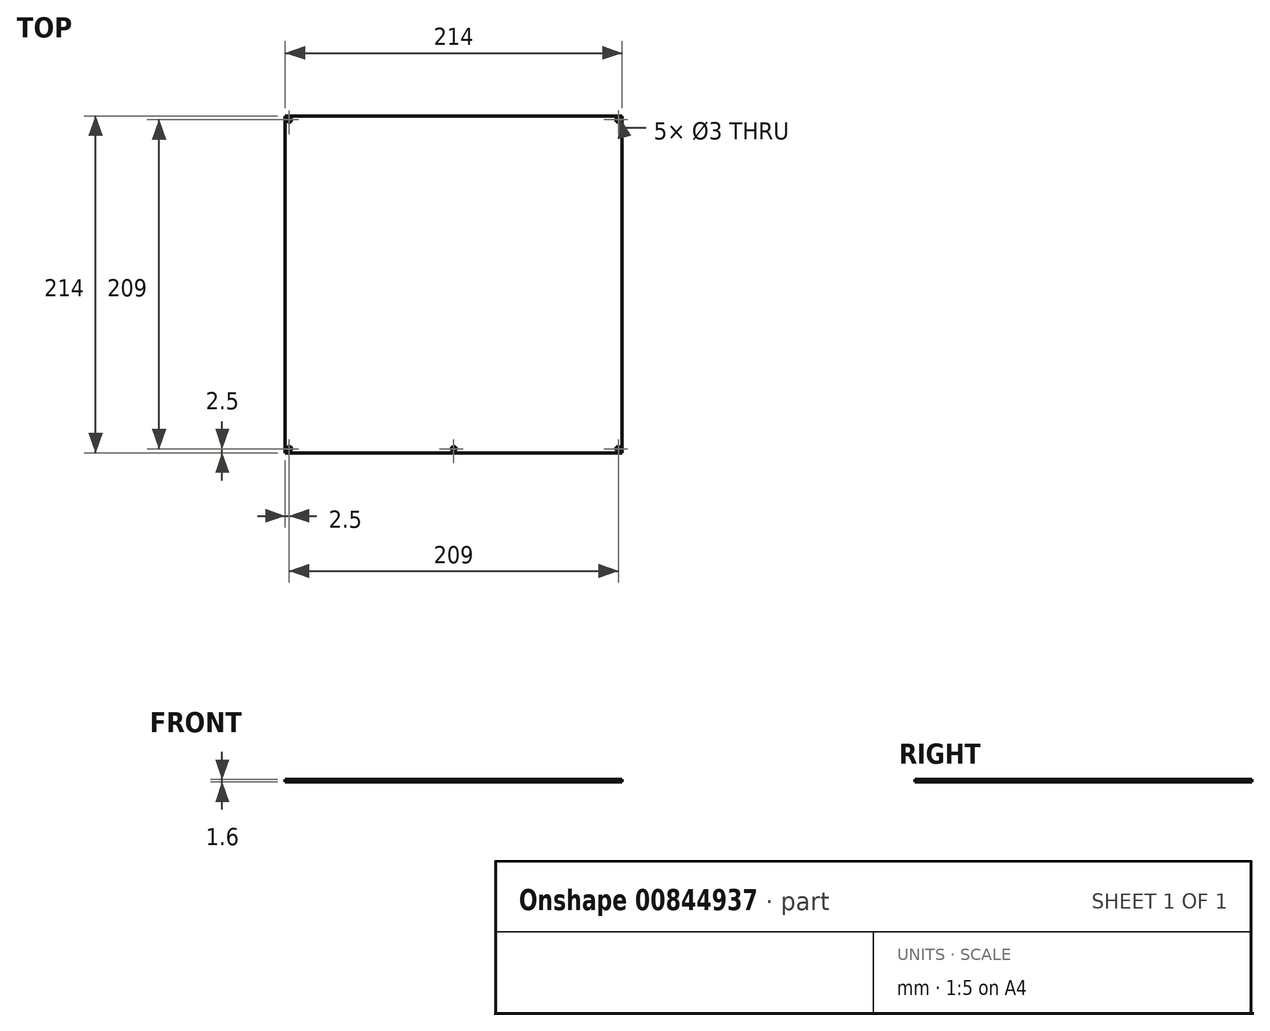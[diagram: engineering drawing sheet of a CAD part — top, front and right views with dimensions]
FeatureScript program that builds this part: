
annotation { "Feature Type Name" : "Feature", "Feature Type Description" : "" }
export const myFeature = defineFeature(function(context is Context, id is Id, definition is map)
    precondition{}
    {
        {
            var Q0;
            Q0=qCreatedBy(makeId("Top.planeOp"),FACE);
            var sketch = newSketch(context, id + "F0", { "sketchPlane" : qUnion([Q0])});
            skLineSegment(sketch, "E0.bottom", {"start": v(0, 0) * mm, "end": v(214, 0) * mm});
            skLineSegment(sketch, "E0.top", {"start": v(0, 214) * mm, "end": v(214, 214) * mm});
            skLineSegment(sketch, "E0.left", {"start": v(0, 0) * mm, "end": v(0, 214) * mm});
            skLineSegment(sketch, "E0.right", {"start": v(214, 0) * mm, "end": v(214, 214) * mm});
            skLineSegment(sketch, "E1.bottom", {"start": v(211.5, 2.5) * mm, "end": v(2.5, 2.5) * mm});
            skLineSegment(sketch, "E1.top", {"start": v(211.5, 211.5) * mm, "end": v(2.5, 211.5) * mm});
            skLineSegment(sketch, "E1.left", {"start": v(211.5, 2.5) * mm, "end": v(211.5, 211.5) * mm});
            skLineSegment(sketch, "E1.right", {"start": v(2.5, 2.5) * mm, "end": v(2.5, 211.5) * mm});
            skPoint(sketch, "E1.middle", {"position": v(107, 107) * mm});
            skPoint(sketch, "E1.middle.positionSnap0", {"position": v(0, 107) * mm});
            skPoint(sketch, "E1.middle.positionSnap1", {"position": v(107, 0) * mm});
            skPoint(sketch, "E1.centerSnap0", {"position": v(0, 107) * mm});
            skPoint(sketch, "E1.centerSnap1", {"position": v(107, 0) * mm});
            skCircle(sketch, "E2", {"center": v(2.5, 211.5) * mm, "radius": 1.5 * mm});
            skCircle(sketch, "E3", {"center": v(211.5, 211.5) * mm, "radius": 1.5 * mm});
            skCircle(sketch, "E4", {"center": v(211.5, 2.5) * mm, "radius": 1.5 * mm});
            skCircle(sketch, "E5", {"center": v(2.5, 2.5) * mm, "radius": 1.5 * mm});
            skCircle(sketch, "E6", {"center": v(107, 2.5) * mm, "radius": 1.5 * mm});
            skSolve(sketch);
        }
        {
            var Q0;
            {var subQ0=sQuery(id+"F0.wireOp",EDGE,"E4");var subQ6=sQuery(id+"F0.wireOp",EDGE,"E1.bottom");var subQ16=makeQuery(id+"F0.imprint","INTERSECT",VERTEX,{"derivedFrom":[subQ6,subQ0]});Q0=makeQuery(id+"F0.imprint","IMPRINT",FACE,{"disambiguationData":[TD([[makeQuery(id+"F0.imprint","IMPRINT",EDGE,{"disambiguationData":[TD([[subQ16,-1.0]])],"derivedFrom":subQ6}),-1.0]])]});}
            var Q1;
            Q1=makeQuery(id+"F0.imprint","IMPRINT",FACE,{"disambiguationData":[TD([[makeQuery(id+"F0.imprint","IMPRINT",EDGE,{"derivedFrom":sQuery(id+"F0.wireOp",EDGE,"E0.bottom")}),1.0]])]});
            extrude(context, id + "F1", {"entities" : qUnion([Q0, Q1]), "depth" : 1.6 * mm, "offsetDistance" : 25 * mm});
        }
    });
